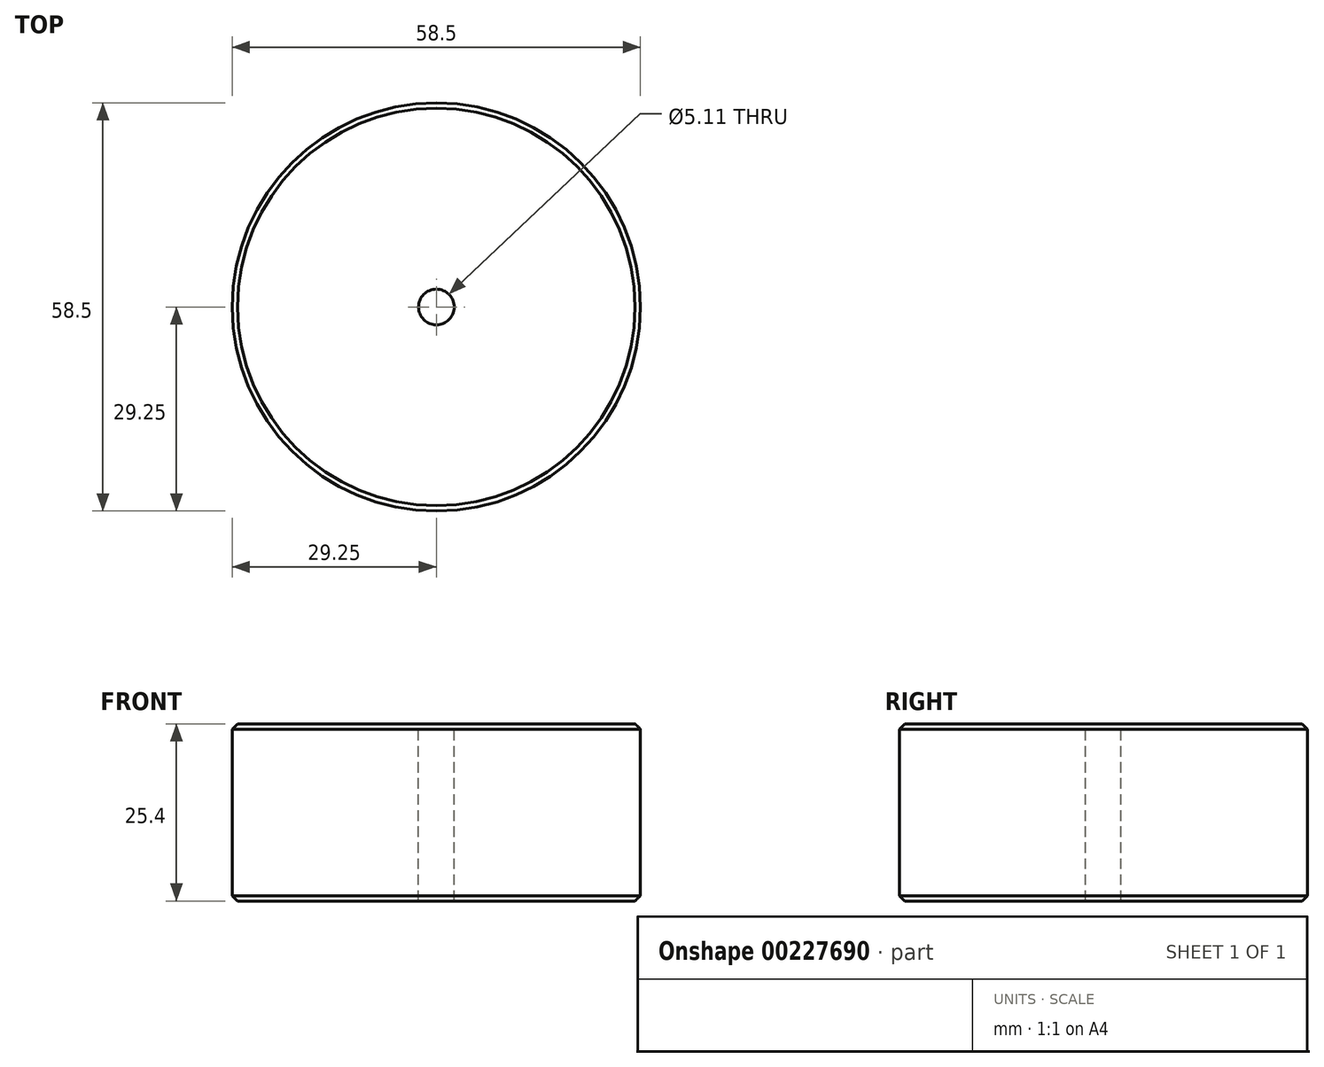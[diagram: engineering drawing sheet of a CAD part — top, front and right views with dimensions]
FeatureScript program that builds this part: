
annotation { "Feature Type Name" : "Feature", "Feature Type Description" : "" }
export const myFeature = defineFeature(function(context is Context, id is Id, definition is map)
    precondition{}
    {
        {
            var Q0;
            Q0=qCreatedBy(makeId("Top.planeOp"),FACE);
            var sketch = newSketch(context, id + "F0", { "sketchPlane" : qUnion([Q0])});
            skCircle(sketch, "E0", {"center": v(0, 0) * mm, "radius": 29.25 * mm});
            skSolve(sketch);
        }
        {
            var Q0;
            Q0 = qSketchRegion(id + "F0", true);
            extrude(context, id + "F1", {"entities" : qUnion([Q0]), "depth" : 25.4 * mm});
        }
        {
            var Q0;
            Q0=makeQuery(id+"F1.opExtrude","CAP_EDGE",EDGE,{"disambiguationData":[OSD([sQuery(id+"F0.wireOp",EDGE,"E0")])],"isStart":false});
            var Q1;
            Q1=makeQuery(id+"F1.opExtrude","CAP_EDGE",EDGE,{"disambiguationData":[OSD([sQuery(id+"F0.wireOp",EDGE,"E0")])],"isStart":true});
            chamfer(context, id + "F2", {"entities" : qUnion([Q0, Q1]), "width" : 0.76 * mm, "tangentPropagation" : true});
        }
        {
            var Q0;
            Q0=makeQuery(id+"F1.opExtrude","CAP_FACE",FACE,{"disambiguationData":[OSD([sQuery(id+"F0.wireOp",EDGE,"E0")])],"isStart":false});
            var sketch = newSketch(context, id + "F3", { "sketchPlane" : qUnion([Q0])});
            skPoint(sketch, "E1", {"position": v(0, 0) * mm});
            skSolve(sketch);
        }
        {
            var Q0;
            Q0=sQuery(id+"F3.wireOp",VERTEX,"E1");
            var Q1;
            Q1=makeQuery(id+"F1.opExtrude","SWEPT_BODY",BODY,{"disambiguationData":[OSD([sQuery(id+"F0.wireOp",EDGE,"E0")])]});
            hole(context, id + "F4", {"style" : HoleStyle.SIMPLE, "endStyle" : HoleEndStyle.THROUGH, "standardTappedOrClearance" : lookupTablePath({ "standard" : "ANSI", "engagement" : "75%", "pitch" : "20 tpi", "size" : "1/4", "type" : "Tapped" }), "standardBlindInLast" : lookupTablePath({ "standard" : "ANSI", "engagement" : "75%", "pitch" : "20 tpi", "size" : "1/4", "type" : "Tapped" }), "holeDiameter" : 5.1 * mm, "locations" : qUnion([Q0]), "scope" : qUnion([Q1]), "isTappedThrough" : true, "majorDiameter" : 6.35 * mm, "showTappedDepth" : true});
        }
    });
